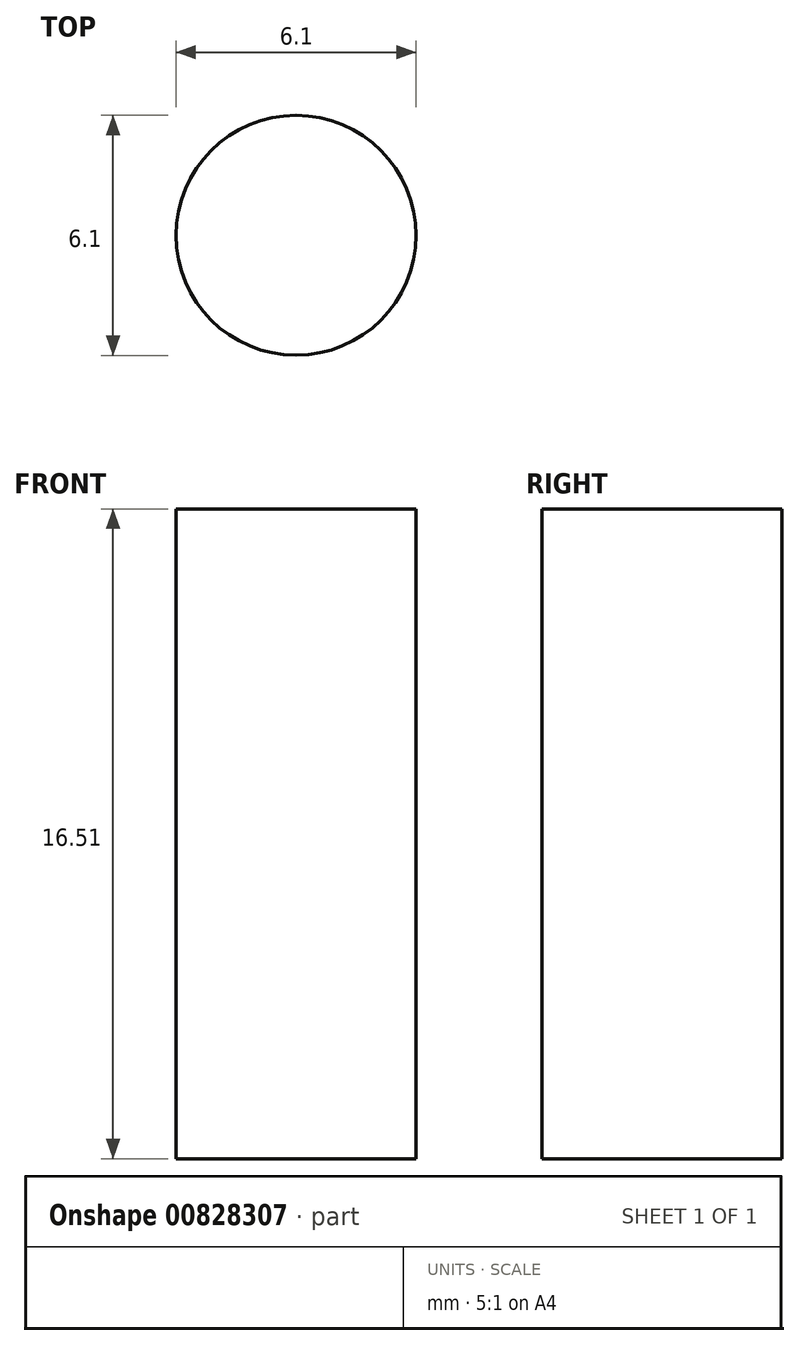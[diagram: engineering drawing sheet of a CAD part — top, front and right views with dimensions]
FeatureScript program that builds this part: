
annotation { "Feature Type Name" : "Feature", "Feature Type Description" : "" }
export const myFeature = defineFeature(function(context is Context, id is Id, definition is map)
    precondition{}
    {
        {
            var Q0;
            Q0=qCreatedBy(makeId("Top.planeOp"),FACE);
            var sketch = newSketch(context, id + "F0", { "sketchPlane" : qUnion([Q0])});
            skCircle(sketch, "E0", {"center": v(0.23, 0) * mm, "radius": 3.05 * mm});
            skSolve(sketch);
        }
        {
            var Q0;
            Q0=makeQuery(id+"F0.imprint","IMPRINT",FACE,{"disambiguationData":[TD([[makeQuery(id+"F0.imprint","IMPRINT",EDGE,{"derivedFrom":sQuery(id+"F0.wireOp",EDGE,"E0")}),1.0]])]});
            extrude(context, id + "F1", {"entities" : qUnion([Q0]), "depth" : 16.5 * mm, "offsetDistance" : 25.4 * mm});
        }
    });
